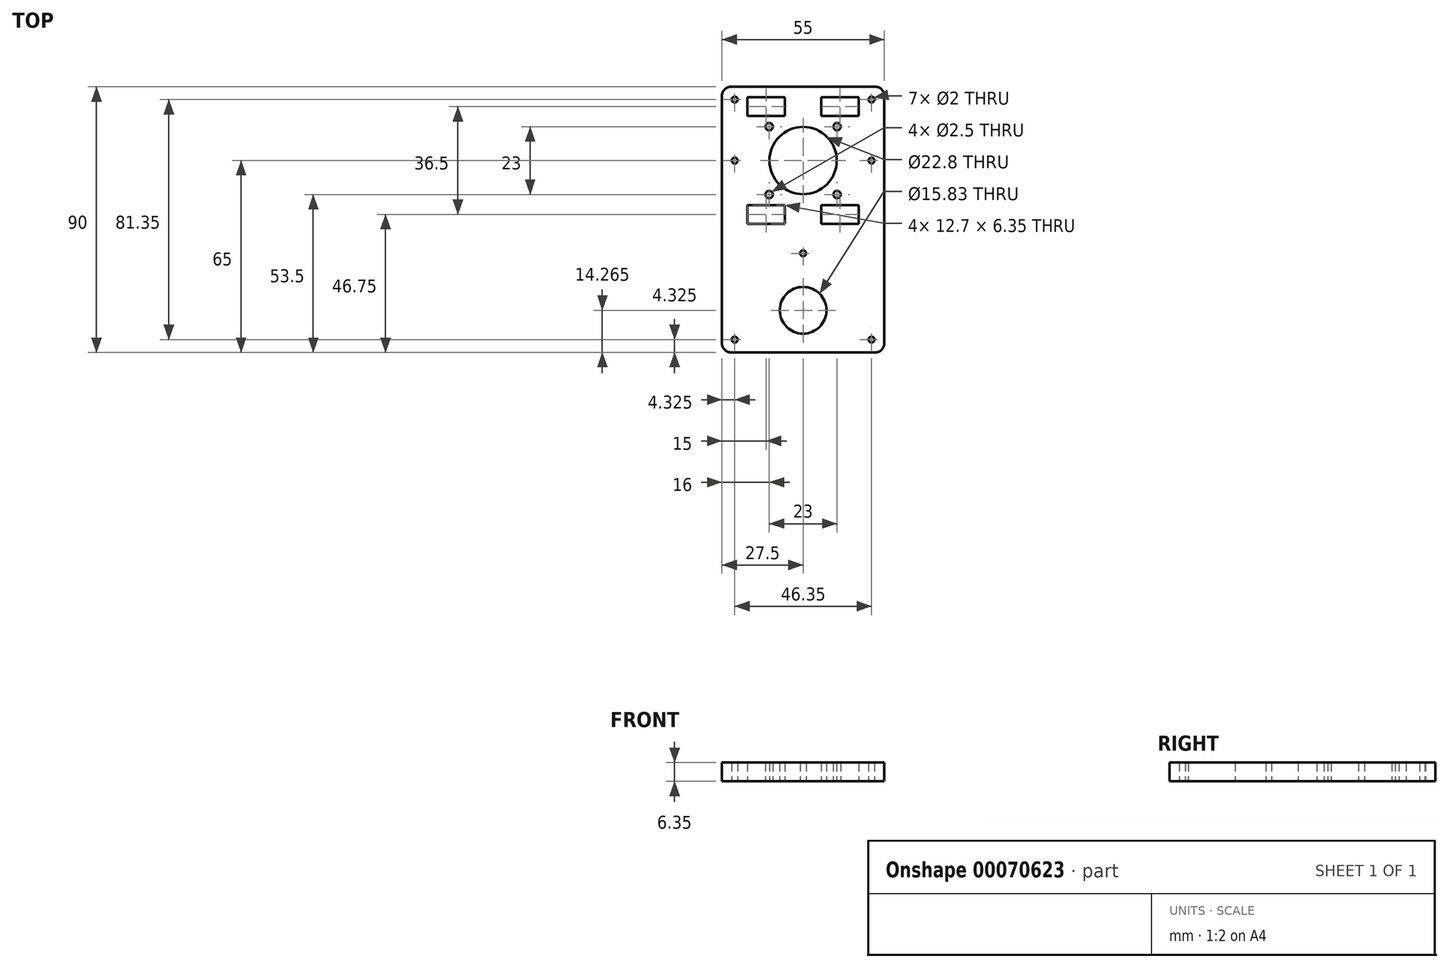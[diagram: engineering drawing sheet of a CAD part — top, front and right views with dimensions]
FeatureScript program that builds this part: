
annotation { "Feature Type Name" : "Feature", "Feature Type Description" : "" }
export const myFeature = defineFeature(function(context is Context, id is Id, definition is map)
    precondition{}
    {
        {
            var Q0;
            Q0=qCreatedBy(makeId("Top.planeOp"),FACE);
            var sketch = newSketch(context, id + "F0", { "sketchPlane" : qUnion([Q0])});
            skCircle(sketch, "E0", {"center": v(0, 0) * mm, "radius": 11.4 * mm});
            skLineSegment(sketch, "E1", {"start": v(0, 0) * mm, "end": v(0, 12.13) * mm});
            skLineSegment(sketch, "E2.bottom", {"start": v(-27.5, 25) * mm, "end": v(27.5, 25) * mm});
            skLineSegment(sketch, "E2.top", {"start": v(-27.5, -65) * mm, "end": v(27.5, -65) * mm});
            skLineSegment(sketch, "E2.left", {"start": v(-27.5, 25) * mm, "end": v(-27.5, -65) * mm});
            skLineSegment(sketch, "E2.right", {"start": v(27.5, 25) * mm, "end": v(27.5, -65) * mm});
            skPoint(sketch, "E3", {"position": v(-11.5, 11.5) * mm});
            skPoint(sketch, "E4.0.1.0", {"position": v(-11.5, -11.5) * mm});
            skPoint(sketch, "E4.1.0.0", {"position": v(11.5, 11.5) * mm});
            skPoint(sketch, "E4.1.1.0", {"position": v(11.5, -11.5) * mm});
            skLineSegment(sketch, "E4.direction1", {"start": v(-11.5, 11.5) * mm, "end": v(11.5, 11.5) * mm, "construction": true});
            skLineSegment(sketch, "E4.direction2", {"start": v(-11.5, 11.5) * mm, "end": v(-11.5, -11.5) * mm, "construction": true});
            skLineSegment(sketch, "E5.bottom", {"start": v(-18.85, 21.43) * mm, "end": v(-6.15, 21.43) * mm});
            skLineSegment(sketch, "E5.top", {"start": v(-18.85, 15.08) * mm, "end": v(-6.15, 15.08) * mm});
            skLineSegment(sketch, "E5.left", {"start": v(-18.85, 21.43) * mm, "end": v(-18.85, 15.07) * mm});
            skLineSegment(sketch, "E5.right", {"start": v(-6.15, 21.43) * mm, "end": v(-6.15, 15.07) * mm});
            skPoint(sketch, "E6", {"position": v(-12.5, 21.43) * mm});
            skLineSegment(sketch, "E7.0.1.0", {"start": v(-18.85, -21.43) * mm, "end": v(-6.15, -21.43) * mm});
            skLineSegment(sketch, "E7.0.1.1", {"start": v(-18.85, -15.07) * mm, "end": v(-6.15, -15.07) * mm});
            skLineSegment(sketch, "E7.0.1.2", {"start": v(-18.85, -15.07) * mm, "end": v(-18.85, -21.43) * mm});
            skLineSegment(sketch, "E7.0.1.3", {"start": v(-6.15, -15.07) * mm, "end": v(-6.15, -21.43) * mm});
            skPoint(sketch, "E7.0.1.4", {"position": v(-12.5, -15.07) * mm});
            skLineSegment(sketch, "E7.1.0.0", {"start": v(6.15, 15.08) * mm, "end": v(18.85, 15.08) * mm});
            skLineSegment(sketch, "E7.1.0.1", {"start": v(6.15, 21.43) * mm, "end": v(18.85, 21.43) * mm});
            skLineSegment(sketch, "E7.1.0.2", {"start": v(6.15, 21.43) * mm, "end": v(6.15, 15.07) * mm});
            skLineSegment(sketch, "E7.1.0.3", {"start": v(18.85, 21.43) * mm, "end": v(18.85, 15.07) * mm});
            skPoint(sketch, "E7.1.0.4", {"position": v(12.5, 21.43) * mm});
            skLineSegment(sketch, "E7.1.1.0", {"start": v(6.15, -21.43) * mm, "end": v(18.85, -21.43) * mm});
            skLineSegment(sketch, "E7.1.1.1", {"start": v(6.15, -15.07) * mm, "end": v(18.85, -15.07) * mm});
            skLineSegment(sketch, "E7.1.1.2", {"start": v(6.15, -15.07) * mm, "end": v(6.15, -21.43) * mm});
            skLineSegment(sketch, "E7.1.1.3", {"start": v(18.85, -15.07) * mm, "end": v(18.85, -21.43) * mm});
            skPoint(sketch, "E7.1.1.4", {"position": v(12.5, -15.07) * mm});
            skLineSegment(sketch, "E7.direction1", {"start": v(-18.85, 15.07) * mm, "end": v(6.15, 15.07) * mm, "construction": true});
            skLineSegment(sketch, "E7.direction2", {"start": v(-18.85, 15.07) * mm, "end": v(-18.85, -21.43) * mm, "construction": true});
            skPoint(sketch, "E8", {"position": v(0, -50.73) * mm});
            skPoint(sketch, "E9", {"position": v(-23.17, -60.67) * mm});
            skPoint(sketch, "E10", {"position": v(-23.17, 20.68) * mm});
            skPoint(sketch, "E11", {"position": v(-23.17, 0) * mm});
            skPoint(sketch, "E12", {"position": v(0, -31.43) * mm});
            skPoint(sketch, "E13.MirrorP", {"position": v(23.17, 20.68) * mm});
            skPoint(sketch, "E14.MirrorP", {"position": v(23.17, 0) * mm});
            skPoint(sketch, "E15.MirrorP", {"position": v(23.17, -60.67) * mm});
            skSolve(sketch);
        }
        {
            var Q0;
            Q0=makeQuery(id+"F0.imprint","IMPRINT",FACE,{"disambiguationData":[TD([[makeQuery(id+"F0.imprint","IMPRINT",EDGE,{"derivedFrom":sQuery(id+"F0.wireOp",EDGE,"E0")}),-1.0]])]});
            extrude(context, id + "F1", {"entities" : qUnion([Q0]), "depth" : 6.35 * mm});
        }
        {
            var Q0;
            Q0=sQuery(id+"F0.wireOp",VERTEX,"E3");
            var Q1;
            Q1=sQuery(id+"F0.wireOp",VERTEX,"E4.1.0.0");
            var Q2;
            Q2=sQuery(id+"F0.wireOp",VERTEX,"E4.1.1.0");
            var Q3;
            Q3=sQuery(id+"F0.wireOp",VERTEX,"E4.0.1.0");
            var Q4;
            Q4=makeQuery(id+"F1.opExtrude","SWEPT_BODY",BODY,{"disambiguationData":[OSD([sQuery(id+"F0.wireOp",EDGE,"E0"),sQuery(id+"F0.wireOp",EDGE,"E2.bottom"),sQuery(id+"F0.wireOp",EDGE,"E2.top"),sQuery(id+"F0.wireOp",EDGE,"E2.left"),sQuery(id+"F0.wireOp",EDGE,"E2.right")])]});
            hole(context, id + "F2", {"style" : HoleStyle.SIMPLE, "endStyle" : HoleEndStyle.THROUGH, "oppositeDirection" : true, "holeDiameter" : 2.5 * mm, "locations" : qUnion([Q0, Q1, Q2, Q3]), "scope" : qUnion([Q4]), "isTappedThrough" : true});
        }
        {
            var Q0;
            Q0=makeQuery(id+"F1.opExtrude","SWEPT_EDGE",EDGE,{"disambiguationData":[OSD([sQuery(id+"F0.wireOp",EDGE,"E2.top"),sQuery(id+"F0.wireOp",EDGE,"E2.left")])]});
            var Q1;
            Q1=makeQuery(id+"F1.opExtrude","SWEPT_EDGE",EDGE,{"disambiguationData":[OSD([sQuery(id+"F0.wireOp",EDGE,"E2.top"),sQuery(id+"F0.wireOp",EDGE,"E2.right")])]});
            var Q2;
            Q2=makeQuery(id+"F1.opExtrude","SWEPT_EDGE",EDGE,{"disambiguationData":[OSD([sQuery(id+"F0.wireOp",EDGE,"E2.bottom"),sQuery(id+"F0.wireOp",EDGE,"E2.right")])]});
            var Q3;
            Q3=makeQuery(id+"F1.opExtrude","SWEPT_EDGE",EDGE,{"disambiguationData":[OSD([sQuery(id+"F0.wireOp",EDGE,"E2.bottom"),sQuery(id+"F0.wireOp",EDGE,"E2.left")])]});
            fillet(context, id + "F3", {"entities" : qUnion([Q0, Q1, Q2, Q3]), "radius" : 3 * mm, "tangentPropagation" : true, "allowEdgeOverflow" : false});
        }
        {
            var Q0;
            Q0=sQuery(id+"F0.wireOp",VERTEX,"E8");
            var Q1;
            Q1=makeQuery(id+"F1.opExtrude","SWEPT_BODY",BODY,{"disambiguationData":[OSD([sQuery(id+"F0.wireOp",EDGE,"E0"),sQuery(id+"F0.wireOp",EDGE,"E2.bottom"),sQuery(id+"F0.wireOp",EDGE,"E2.top"),sQuery(id+"F0.wireOp",EDGE,"E2.left"),sQuery(id+"F0.wireOp",EDGE,"E2.right"),sQuery(id+"F0.wireOp",EDGE,"E5.bottom"),sQuery(id+"F0.wireOp",EDGE,"E5.top"),sQuery(id+"F0.wireOp",EDGE,"E5.left"),sQuery(id+"F0.wireOp",EDGE,"E5.right"),sQuery(id+"F0.wireOp",EDGE,"E7.0.1.0"),sQuery(id+"F0.wireOp",EDGE,"E7.0.1.1"),sQuery(id+"F0.wireOp",EDGE,"E7.0.1.2"),sQuery(id+"F0.wireOp",EDGE,"E7.0.1.3"),sQuery(id+"F0.wireOp",EDGE,"E7.1.0.0"),sQuery(id+"F0.wireOp",EDGE,"E7.1.0.1"),sQuery(id+"F0.wireOp",EDGE,"E7.1.0.2"),sQuery(id+"F0.wireOp",EDGE,"E7.1.0.3"),sQuery(id+"F0.wireOp",EDGE,"E7.1.1.0"),sQuery(id+"F0.wireOp",EDGE,"E7.1.1.1"),sQuery(id+"F0.wireOp",EDGE,"E7.1.1.2"),sQuery(id+"F0.wireOp",EDGE,"E7.1.1.3")])]});
            hole(context, id + "F4", {"style" : HoleStyle.SIMPLE, "endStyle" : HoleEndStyle.THROUGH, "oppositeDirection" : true, "holeDiameter" : 15.83 * mm, "locations" : qUnion([Q0]), "scope" : qUnion([Q1]), "isTappedThrough" : true});
        }
        {
            var Q0;
            Q0=sQuery(id+"F0.wireOp",VERTEX,"E10");
            var Q1;
            Q1=sQuery(id+"F0.wireOp",VERTEX,"E13.MirrorP");
            var Q2;
            Q2=sQuery(id+"F0.wireOp",VERTEX,"E14.MirrorP");
            var Q3;
            Q3=sQuery(id+"F0.wireOp",VERTEX,"E11");
            var Q4;
            Q4=sQuery(id+"F0.wireOp",VERTEX,"E9");
            var Q5;
            Q5=sQuery(id+"F0.wireOp",VERTEX,"E15.MirrorP");
            var Q6;
            Q6=sQuery(id+"F0.wireOp",VERTEX,"E12");
            var Q7;
            Q7=makeQuery(id+"F1.opExtrude","SWEPT_BODY",BODY,{"disambiguationData":[OSD([sQuery(id+"F0.wireOp",EDGE,"E0"),sQuery(id+"F0.wireOp",EDGE,"E2.bottom"),sQuery(id+"F0.wireOp",EDGE,"E2.top"),sQuery(id+"F0.wireOp",EDGE,"E2.left"),sQuery(id+"F0.wireOp",EDGE,"E2.right"),sQuery(id+"F0.wireOp",EDGE,"E5.bottom"),sQuery(id+"F0.wireOp",EDGE,"E5.top"),sQuery(id+"F0.wireOp",EDGE,"E5.left"),sQuery(id+"F0.wireOp",EDGE,"E5.right"),sQuery(id+"F0.wireOp",EDGE,"E7.0.1.0"),sQuery(id+"F0.wireOp",EDGE,"E7.0.1.1"),sQuery(id+"F0.wireOp",EDGE,"E7.0.1.2"),sQuery(id+"F0.wireOp",EDGE,"E7.0.1.3"),sQuery(id+"F0.wireOp",EDGE,"E7.1.0.0"),sQuery(id+"F0.wireOp",EDGE,"E7.1.0.1"),sQuery(id+"F0.wireOp",EDGE,"E7.1.0.2"),sQuery(id+"F0.wireOp",EDGE,"E7.1.0.3"),sQuery(id+"F0.wireOp",EDGE,"E7.1.1.0"),sQuery(id+"F0.wireOp",EDGE,"E7.1.1.1"),sQuery(id+"F0.wireOp",EDGE,"E7.1.1.2"),sQuery(id+"F0.wireOp",EDGE,"E7.1.1.3")])]});
            hole(context, id + "F5", {"style" : HoleStyle.SIMPLE, "endStyle" : HoleEndStyle.THROUGH, "oppositeDirection" : true, "holeDiameter" : 2 * mm, "locations" : qUnion([Q0, Q1, Q2, Q3, Q4, Q5, Q6]), "scope" : qUnion([Q7]), "isTappedThrough" : true});
        }
    });
